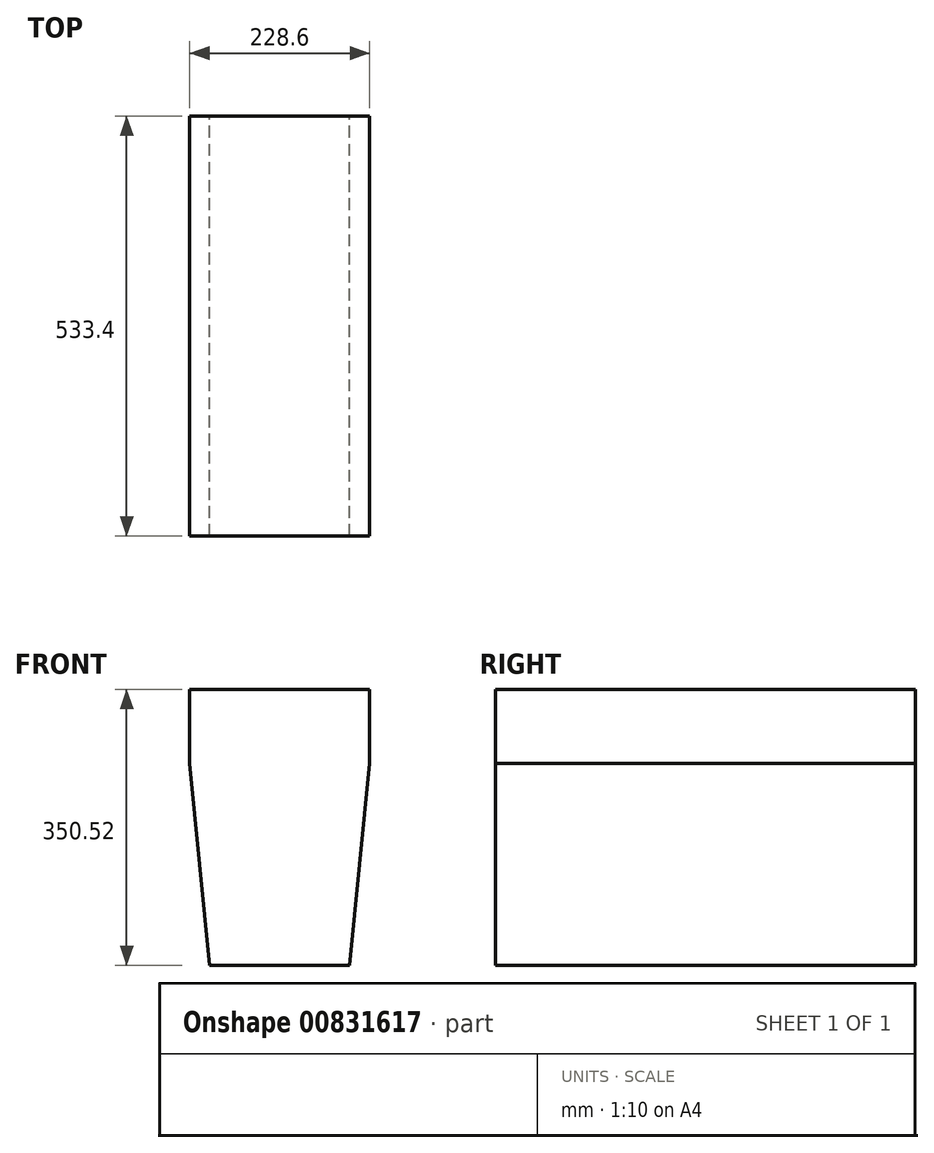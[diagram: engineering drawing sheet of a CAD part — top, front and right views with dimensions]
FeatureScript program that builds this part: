
annotation { "Feature Type Name" : "Feature", "Feature Type Description" : "" }
export const myFeature = defineFeature(function(context is Context, id is Id, definition is map)
    precondition{}
    {
        {
            var Q0;
            Q0=qCreatedBy(makeId("Front.planeOp"),FACE);
            var sketch = newSketch(context, id + "F0", { "sketchPlane" : qUnion([Q0])});
            skLineSegment(sketch, "E0", {"start": v(-105, 227.48) * mm, "end": v(123.6, 227.48) * mm});
            skLineSegment(sketch, "E1", {"start": v(123.6, 227.48) * mm, "end": v(123.6, 133.5) * mm});
            skLineSegment(sketch, "E2", {"start": v(123.6, 133.5) * mm, "end": v(98.2, -123.04) * mm});
            skLineSegment(sketch, "E3", {"start": v(98.2, -123.04) * mm, "end": v(-79.6, -123.04) * mm});
            skLineSegment(sketch, "E4", {"start": v(-79.6, -123.04) * mm, "end": v(-105, 133.5) * mm});
            skLineSegment(sketch, "E5", {"start": v(-105, 133.5) * mm, "end": v(-105, 227.48) * mm});
            skSolve(sketch);
        }
        {
            var Q0;
            Q0 = qSketchRegion(id + "F0", true);
            extrude(context, id + "F1", {"entities" : qUnion([Q0]), "depth" : 533.4 * mm, "offsetDistance" : 25.4 * mm});
        }
    });
